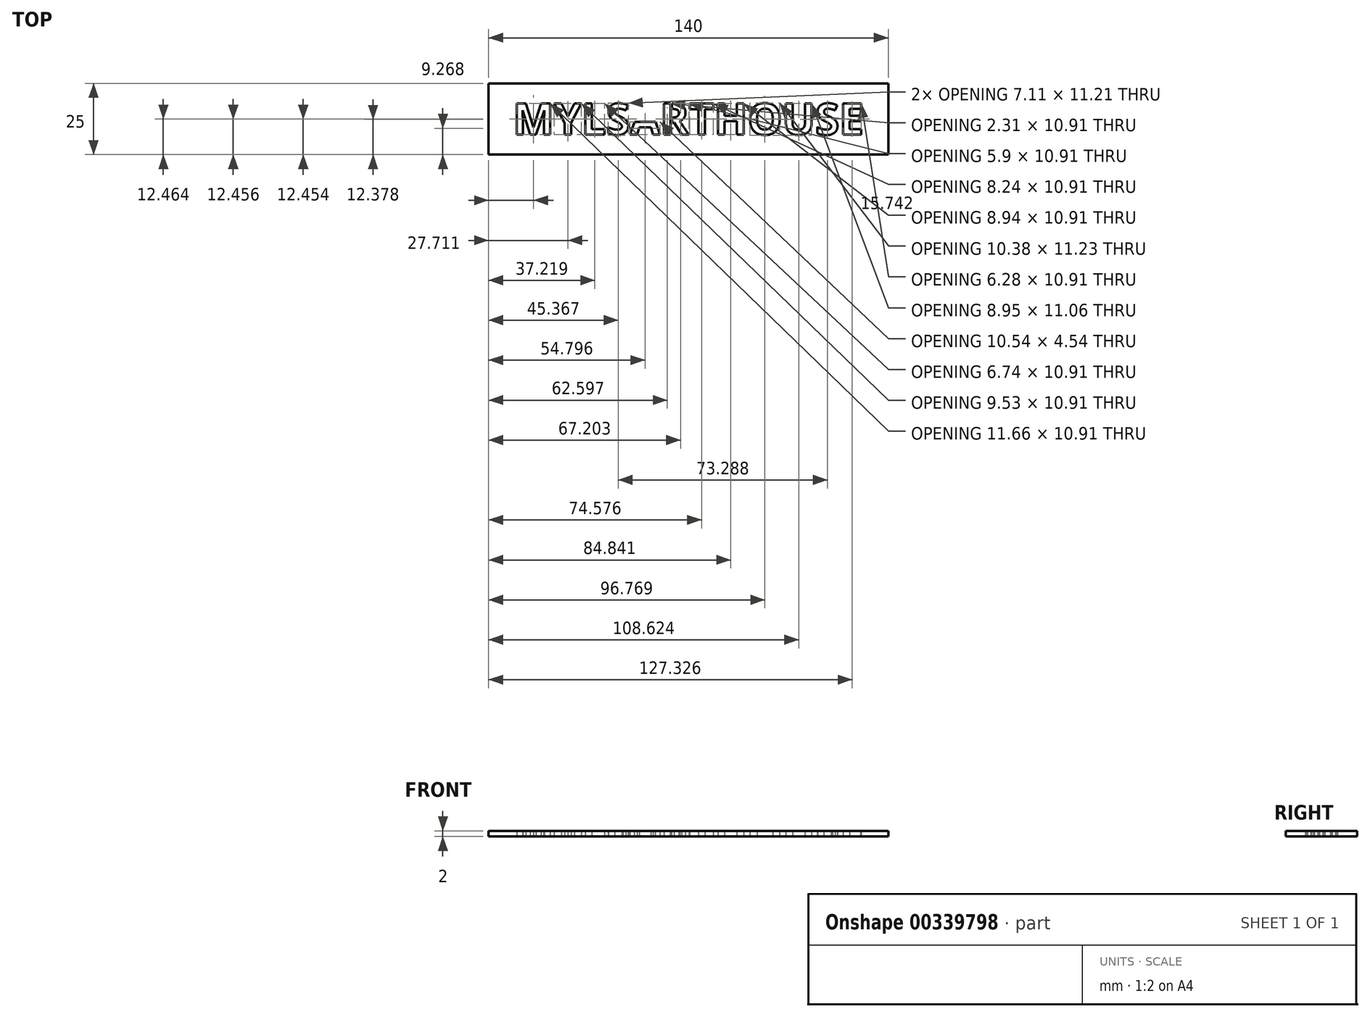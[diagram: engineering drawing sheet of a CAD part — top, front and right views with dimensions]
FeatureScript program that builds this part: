
annotation { "Feature Type Name" : "Feature", "Feature Type Description" : "" }
export const myFeature = defineFeature(function(context is Context, id is Id, definition is map)
    precondition{}
    {
        {
            var Q0;
            Q0=qCreatedBy(makeId("Top.planeOp"),FACE);
            var sketch = newSketch(context, id + "F0", { "sketchPlane" : qUnion([Q0])});
            skText(sketch, "E0", { "text": "MYLSARTHOUSE", "fontName": "OpenSans-Bold.ttf"});
            skLineSegment(sketch, "E1.bottom", {"start": v(70, -12.5) * mm, "end": v(-70, -12.5) * mm});
            skLineSegment(sketch, "E1.top", {"start": v(70, 12.5) * mm, "end": v(-70, 12.5) * mm});
            skLineSegment(sketch, "E1.left", {"start": v(70, -12.5) * mm, "end": v(70, 12.5) * mm});
            skLineSegment(sketch, "E1.right", {"start": v(-70, -12.5) * mm, "end": v(-70, 12.5) * mm});
            skPoint(sketch, "E1.middle", {"position": v(0, 0) * mm});
            const initialGuessF0  = {"E0": [-0.06146, -0.0055, 1, 0, 0.011]};
            skSetInitialGuess(sketch, initialGuessF0);
            skSolve(sketch);
        }
        {
            var Q0;
            Q0=makeQuery(id+"F0.imprint","IMPRINT",FACE,{"disambiguationData":[TD([[makeQuery(id+"F0.imprint","IMPRINT",EDGE,{"derivedFrom":sQuery(id+"F0.wireOp",EDGE,"E0.sketch_text.stroke-0")}),1.0]])]});
            var Q1;
            Q1=makeQuery(id+"F0.imprint","IMPRINT",FACE,{"disambiguationData":[TD([[makeQuery(id+"F0.imprint","IMPRINT",EDGE,{"derivedFrom":sQuery(id+"F0.wireOp",EDGE,"E0.sketch_text.stroke-74")}),1.0]])]});
            var Q2;
            Q2=makeQuery(id+"F0.imprint","IMPRINT",FACE,{"disambiguationData":[TD([[makeQuery(id+"F0.imprint","IMPRINT",EDGE,{"derivedFrom":sQuery(id+"F0.wireOp",EDGE,"E0.sketch_text.stroke-70")}),1.0]])]});
            var Q3;
            Q3 = qSketchRegion(id + "F0", true);
            var Q4;
            Q4=makeQuery(id+"F0.imprint","IMPRINT",FACE,{"disambiguationData":[TD([[makeQuery(id+"F0.imprint","IMPRINT",EDGE,{"derivedFrom":sQuery(id+"F0.wireOp",EDGE,"E0.sketch_text.stroke-121")}),1.0]])]});
            extrude(context, id + "F1", {"entities" : qUnion([Q0, Q1, Q2, Q3, Q4]), "depth" : 2 * mm});
        }
        {
            var Q0;
            Q0=makeQuery(id+"F1.opExtrude","CAP_FACE",FACE,{"disambiguationData":[OSD([sQuery(id+"F0.wireOp",EDGE,"E0.sketch_text.stroke-0"),sQuery(id+"F0.wireOp",EDGE,"E0.sketch_text.stroke-1"),sQuery(id+"F0.wireOp",EDGE,"E0.sketch_text.stroke-2"),sQuery(id+"F0.wireOp",EDGE,"E0.sketch_text.stroke-3"),sQuery(id+"F0.wireOp",EDGE,"E0.sketch_text.stroke-4"),sQuery(id+"F0.wireOp",EDGE,"E0.sketch_text.stroke-5"),sQuery(id+"F0.wireOp",EDGE,"E0.sketch_text.stroke-6"),sQuery(id+"F0.wireOp",EDGE,"E0.sketch_text.stroke-7"),sQuery(id+"F0.wireOp",EDGE,"E0.sketch_text.stroke-8"),sQuery(id+"F0.wireOp",EDGE,"E0.sketch_text.stroke-9"),sQuery(id+"F0.wireOp",EDGE,"E0.sketch_text.stroke-10"),sQuery(id+"F0.wireOp",EDGE,"E0.sketch_text.stroke-11"),sQuery(id+"F0.wireOp",EDGE,"E0.sketch_text.stroke-12"),sQuery(id+"F0.wireOp",EDGE,"E0.sketch_text.stroke-13"),sQuery(id+"F0.wireOp",EDGE,"E0.sketch_text.stroke-14"),sQuery(id+"F0.wireOp",EDGE,"E0.sketch_text.stroke-15"),sQuery(id+"F0.wireOp",EDGE,"E0.sketch_text.stroke-16"),sQuery(id+"F0.wireOp",EDGE,"E0.sketch_text.stroke-17"),sQuery(id+"F0.wireOp",EDGE,"E0.sketch_text.stroke-18"),sQuery(id+"F0.wireOp",EDGE,"E0.sketch_text.stroke-19"),sQuery(id+"F0.wireOp",EDGE,"E0.sketch_text.stroke-20"),sQuery(id+"F0.wireOp",EDGE,"E0.sketch_text.stroke-21"),sQuery(id+"F0.wireOp",EDGE,"E0.sketch_text.stroke-22"),sQuery(id+"F0.wireOp",EDGE,"E0.sketch_text.stroke-23"),sQuery(id+"F0.wireOp",EDGE,"E0.sketch_text.stroke-24"),sQuery(id+"F0.wireOp",EDGE,"E0.sketch_text.stroke-25"),sQuery(id+"F0.wireOp",EDGE,"E0.sketch_text.stroke-26"),sQuery(id+"F0.wireOp",EDGE,"E0.sketch_text.stroke-27"),sQuery(id+"F0.wireOp",EDGE,"E0.sketch_text.stroke-28"),sQuery(id+"F0.wireOp",EDGE,"E0.sketch_text.stroke-29"),sQuery(id+"F0.wireOp",EDGE,"E0.sketch_text.stroke-30"),sQuery(id+"F0.wireOp",EDGE,"E0.sketch_text.stroke-31"),sQuery(id+"F0.wireOp",EDGE,"E0.sketch_text.stroke-32"),sQuery(id+"F0.wireOp",EDGE,"E0.sketch_text.stroke-33"),sQuery(id+"F0.wireOp",EDGE,"E0.sketch_text.stroke-34"),sQuery(id+"F0.wireOp",EDGE,"E0.sketch_text.stroke-35"),sQuery(id+"F0.wireOp",EDGE,"E0.sketch_text.stroke-36"),sQuery(id+"F0.wireOp",EDGE,"E0.sketch_text.stroke-37"),sQuery(id+"F0.wireOp",EDGE,"E0.sketch_text.stroke-38"),sQuery(id+"F0.wireOp",EDGE,"E0.sketch_text.stroke-39"),sQuery(id+"F0.wireOp",EDGE,"E0.sketch_text.stroke-40"),sQuery(id+"F0.wireOp",EDGE,"E0.sketch_text.stroke-41"),sQuery(id+"F0.wireOp",EDGE,"E0.sketch_text.stroke-42"),sQuery(id+"F0.wireOp",EDGE,"E0.sketch_text.stroke-43"),sQuery(id+"F0.wireOp",EDGE,"E0.sketch_text.stroke-44"),sQuery(id+"F0.wireOp",EDGE,"E0.sketch_text.stroke-45"),sQuery(id+"F0.wireOp",EDGE,"E0.sketch_text.stroke-46"),sQuery(id+"F0.wireOp",EDGE,"E0.sketch_text.stroke-47"),sQuery(id+"F0.wireOp",EDGE,"E0.sketch_text.stroke-48"),sQuery(id+"F0.wireOp",EDGE,"E0.sketch_text.stroke-49"),sQuery(id+"F0.wireOp",EDGE,"E0.sketch_text.stroke-50"),sQuery(id+"F0.wireOp",EDGE,"E0.sketch_text.stroke-51"),sQuery(id+"F0.wireOp",EDGE,"E0.sketch_text.stroke-52"),sQuery(id+"F0.wireOp",EDGE,"E0.sketch_text.stroke-53"),sQuery(id+"F0.wireOp",EDGE,"E0.sketch_text.stroke-54"),sQuery(id+"F0.wireOp",EDGE,"E0.sketch_text.stroke-55"),sQuery(id+"F0.wireOp",EDGE,"E0.sketch_text.stroke-56"),sQuery(id+"F0.wireOp",EDGE,"E0.sketch_text.stroke-57"),sQuery(id+"F0.wireOp",EDGE,"E0.sketch_text.stroke-58"),sQuery(id+"F0.wireOp",EDGE,"E0.sketch_text.stroke-59"),sQuery(id+"F0.wireOp",EDGE,"E0.sketch_text.stroke-60"),sQuery(id+"F0.wireOp",EDGE,"E0.sketch_text.stroke-61"),sQuery(id+"F0.wireOp",EDGE,"E0.sketch_text.stroke-62"),sQuery(id+"F0.wireOp",EDGE,"E0.sketch_text.stroke-63"),sQuery(id+"F0.wireOp",EDGE,"E0.sketch_text.stroke-64"),sQuery(id+"F0.wireOp",EDGE,"E0.sketch_text.stroke-65"),sQuery(id+"F0.wireOp",EDGE,"E0.sketch_text.stroke-66"),sQuery(id+"F0.wireOp",EDGE,"E0.sketch_text.stroke-67"),sQuery(id+"F0.wireOp",EDGE,"E0.sketch_text.stroke-68"),sQuery(id+"F0.wireOp",EDGE,"E0.sketch_text.stroke-69"),sQuery(id+"F0.wireOp",EDGE,"E0.sketch_text.stroke-81"),sQuery(id+"F0.wireOp",EDGE,"E0.sketch_text.stroke-82"),sQuery(id+"F0.wireOp",EDGE,"E0.sketch_text.stroke-83"),sQuery(id+"F0.wireOp",EDGE,"E0.sketch_text.stroke-84"),sQuery(id+"F0.wireOp",EDGE,"E0.sketch_text.stroke-85"),sQuery(id+"F0.wireOp",EDGE,"E0.sketch_text.stroke-86"),sQuery(id+"F0.wireOp",EDGE,"E0.sketch_text.stroke-87"),sQuery(id+"F0.wireOp",EDGE,"E0.sketch_text.stroke-88"),sQuery(id+"F0.wireOp",EDGE,"E0.sketch_text.stroke-89"),sQuery(id+"F0.wireOp",EDGE,"E0.sketch_text.stroke-90"),sQuery(id+"F0.wireOp",EDGE,"E0.sketch_text.stroke-91"),sQuery(id+"F0.wireOp",EDGE,"E0.sketch_text.stroke-92"),sQuery(id+"F0.wireOp",EDGE,"E0.sketch_text.stroke-93"),sQuery(id+"F0.wireOp",EDGE,"E0.sketch_text.stroke-94"),sQuery(id+"F0.wireOp",EDGE,"E0.sketch_text.stroke-95"),sQuery(id+"F0.wireOp",EDGE,"E0.sketch_text.stroke-96"),sQuery(id+"F0.wireOp",EDGE,"E0.sketch_text.stroke-97"),sQuery(id+"F0.wireOp",EDGE,"E0.sketch_text.stroke-98"),sQuery(id+"F0.wireOp",EDGE,"E0.sketch_text.stroke-99"),sQuery(id+"F0.wireOp",EDGE,"E0.sketch_text.stroke-100"),sQuery(id+"F0.wireOp",EDGE,"E0.sketch_text.stroke-101"),sQuery(id+"F0.wireOp",EDGE,"E0.sketch_text.stroke-102"),sQuery(id+"F0.wireOp",EDGE,"E0.sketch_text.stroke-103"),sQuery(id+"F0.wireOp",EDGE,"E0.sketch_text.stroke-104"),sQuery(id+"F0.wireOp",EDGE,"E0.sketch_text.stroke-105"),sQuery(id+"F0.wireOp",EDGE,"E0.sketch_text.stroke-106"),sQuery(id+"F0.wireOp",EDGE,"E0.sketch_text.stroke-107"),sQuery(id+"F0.wireOp",EDGE,"E0.sketch_text.stroke-108"),sQuery(id+"F0.wireOp",EDGE,"E0.sketch_text.stroke-109"),sQuery(id+"F0.wireOp",EDGE,"E0.sketch_text.stroke-110"),sQuery(id+"F0.wireOp",EDGE,"E0.sketch_text.stroke-111"),sQuery(id+"F0.wireOp",EDGE,"E0.sketch_text.stroke-112"),sQuery(id+"F0.wireOp",EDGE,"E0.sketch_text.stroke-113"),sQuery(id+"F0.wireOp",EDGE,"E0.sketch_text.stroke-114"),sQuery(id+"F0.wireOp",EDGE,"E0.sketch_text.stroke-115"),sQuery(id+"F0.wireOp",EDGE,"E0.sketch_text.stroke-116"),sQuery(id+"F0.wireOp",EDGE,"E0.sketch_text.stroke-117"),sQuery(id+"F0.wireOp",EDGE,"E0.sketch_text.stroke-118"),sQuery(id+"F0.wireOp",EDGE,"E0.sketch_text.stroke-119"),sQuery(id+"F0.wireOp",EDGE,"E0.sketch_text.stroke-120"),sQuery(id+"F0.wireOp",EDGE,"E0.sketch_text.stroke-127"),sQuery(id+"F0.wireOp",EDGE,"E0.sketch_text.stroke-128"),sQuery(id+"F0.wireOp",EDGE,"E0.sketch_text.stroke-129"),sQuery(id+"F0.wireOp",EDGE,"E0.sketch_text.stroke-130"),sQuery(id+"F0.wireOp",EDGE,"E0.sketch_text.stroke-131"),sQuery(id+"F0.wireOp",EDGE,"E0.sketch_text.stroke-132"),sQuery(id+"F0.wireOp",EDGE,"E0.sketch_text.stroke-133"),sQuery(id+"F0.wireOp",EDGE,"E0.sketch_text.stroke-134"),sQuery(id+"F0.wireOp",EDGE,"E0.sketch_text.stroke-135"),sQuery(id+"F0.wireOp",EDGE,"E0.sketch_text.stroke-136"),sQuery(id+"F0.wireOp",EDGE,"E0.sketch_text.stroke-137"),sQuery(id+"F0.wireOp",EDGE,"E0.sketch_text.stroke-138"),sQuery(id+"F0.wireOp",EDGE,"E0.sketch_text.stroke-139"),sQuery(id+"F0.wireOp",EDGE,"E0.sketch_text.stroke-140"),sQuery(id+"F0.wireOp",EDGE,"E0.sketch_text.stroke-141"),sQuery(id+"F0.wireOp",EDGE,"E0.sketch_text.stroke-142"),sQuery(id+"F0.wireOp",EDGE,"E0.sketch_text.stroke-143"),sQuery(id+"F0.wireOp",EDGE,"E0.sketch_text.stroke-144"),sQuery(id+"F0.wireOp",EDGE,"E0.sketch_text.stroke-145"),sQuery(id+"F0.wireOp",EDGE,"E0.sketch_text.stroke-146"),sQuery(id+"F0.wireOp",EDGE,"E0.sketch_text.stroke-147"),sQuery(id+"F0.wireOp",EDGE,"E0.sketch_text.stroke-148"),sQuery(id+"F0.wireOp",EDGE,"E0.sketch_text.stroke-149"),sQuery(id+"F0.wireOp",EDGE,"E0.sketch_text.stroke-150"),sQuery(id+"F0.wireOp",EDGE,"E0.sketch_text.stroke-151"),sQuery(id+"F0.wireOp",EDGE,"E0.sketch_text.stroke-152"),sQuery(id+"F0.wireOp",EDGE,"E0.sketch_text.stroke-153"),sQuery(id+"F0.wireOp",EDGE,"E0.sketch_text.stroke-154"),sQuery(id+"F0.wireOp",EDGE,"E0.sketch_text.stroke-155"),sQuery(id+"F0.wireOp",EDGE,"E0.sketch_text.stroke-156"),sQuery(id+"F0.wireOp",EDGE,"E0.sketch_text.stroke-157"),sQuery(id+"F0.wireOp",EDGE,"E0.sketch_text.stroke-158"),sQuery(id+"F0.wireOp",EDGE,"E0.sketch_text.stroke-159"),sQuery(id+"F0.wireOp",EDGE,"E0.sketch_text.stroke-160"),sQuery(id+"F0.wireOp",EDGE,"E0.sketch_text.stroke-161"),sQuery(id+"F0.wireOp",EDGE,"E0.sketch_text.stroke-162"),sQuery(id+"F0.wireOp",EDGE,"E0.sketch_text.stroke-163"),sQuery(id+"F0.wireOp",EDGE,"E0.sketch_text.stroke-164"),sQuery(id+"F0.wireOp",EDGE,"E0.sketch_text.stroke-165"),sQuery(id+"F0.wireOp",EDGE,"E0.sketch_text.stroke-166"),sQuery(id+"F0.wireOp",EDGE,"E0.sketch_text.stroke-167"),sQuery(id+"F0.wireOp",EDGE,"E0.sketch_text.stroke-168"),sQuery(id+"F0.wireOp",EDGE,"E0.sketch_text.stroke-169"),sQuery(id+"F0.wireOp",EDGE,"E0.sketch_text.stroke-170"),sQuery(id+"F0.wireOp",EDGE,"E0.sketch_text.stroke-171"),sQuery(id+"F0.wireOp",EDGE,"E0.sketch_text.stroke-172"),sQuery(id+"F0.wireOp",EDGE,"E0.sketch_text.stroke-173"),sQuery(id+"F0.wireOp",EDGE,"E0.sketch_text.stroke-174"),sQuery(id+"F0.wireOp",EDGE,"E0.sketch_text.stroke-175"),sQuery(id+"F0.wireOp",EDGE,"E0.sketch_text.stroke-176"),sQuery(id+"F0.wireOp",EDGE,"E0.sketch_text.stroke-177"),sQuery(id+"F0.wireOp",EDGE,"E0.sketch_text.stroke-178"),sQuery(id+"F0.wireOp",EDGE,"E0.sketch_text.stroke-179"),sQuery(id+"F0.wireOp",EDGE,"E0.sketch_text.stroke-180"),sQuery(id+"F0.wireOp",EDGE,"E0.sketch_text.stroke-181"),sQuery(id+"F0.wireOp",EDGE,"E1.bottom"),sQuery(id+"F0.wireOp",EDGE,"E1.top"),sQuery(id+"F0.wireOp",EDGE,"E1.left"),sQuery(id+"F0.wireOp",EDGE,"E1.right")])],"isStart":false});
            var sketch = newSketch(context, id + "F2", { "sketchPlane" : qUnion([Q0])});
            skLineSegment(sketch, "E2.0", {"start": v(-16.6, -0.96) * mm, "end": v(-13.77, -0.96) * mm});
            skLineSegment(sketch, "E3.0", {"start": v(-13.8, 5.45) * mm, "end": v(-9.93, -5.5) * mm});
            skLineSegment(sketch, "E4.0", {"start": v(-20.47, -5.5) * mm, "end": v(-16.62, 5.45) * mm});
            skLineSegment(sketch, "E5.0", {"start": v(-16.62, 5.45) * mm, "end": v(-13.8, 5.45) * mm});
            skLineSegment(sketch, "E6.0.0", {"start": v(-5.54, 3.51) * mm, "end": v(-6.25, 3.51) * mm});
            skLineSegment(sketch, "E6.0.1", {"start": v(-6.25, 3.51) * mm, "end": v(-6.25, 0.57) * mm});
            skLineSegment(sketch, "E6.0.2", {"start": v(-6.25, 0.57) * mm, "end": v(-5.5, 0.57) * mm});
            skFitSpline(sketch, "E6.0.3", {"points": [v(-5.5, 0.57) * mm, v(-4.4, 0.57) * mm, v(-3.88, 0.93) * mm]});
            skFitSpline(sketch, "E6.0.4", {"points": [v(-3.88, 0.93) * mm, v(-3.36, 1.3) * mm, v(-3.36, 2.08) * mm]});
            skFitSpline(sketch, "E6.0.5", {"points": [v(-3.36, 2.08) * mm, v(-3.36, 2.86) * mm, v(-3.9, 3.18) * mm]});
            skFitSpline(sketch, "E6.0.6", {"points": [v(-3.9, 3.18) * mm, v(-4.43, 3.51) * mm, v(-5.54, 3.51) * mm]});
            skFitSpline(sketch, "E7.0.0", {"points": [v(-15.2, 3.76) * mm, v(-15.45, 2.8) * mm, v(-16.6, -0.96) * mm]});
            skFitSpline(sketch, "E7.0.2", {"points": [v(-13.77, -0.96) * mm, v(-14.86, 2.56) * mm, v(-15, 3.03) * mm]});
            skFitSpline(sketch, "E7.0.3", {"points": [v(-15, 3.03) * mm, v(-15.14, 3.5) * mm, v(-15.2, 3.76) * mm]});
            skLineSegment(sketch, "E8.0", {"start": v(-5.02, -1.32) * mm, "end": v(-6.25, -1.32) * mm});
            skFitSpline(sketch, "E9.0", {"points": [v(-2.1, 4.6) * mm, v(-1.03, 3.79) * mm, v(-1.03, 2.14) * mm]});
            skFitSpline(sketch, "E10.0", {"points": [v(-1.03, 2.14) * mm, v(-1.03, 1.18) * mm, v(-1.55, 0.43) * mm]});
            skLineSegment(sketch, "E11.0", {"start": v(-8.56, 5.4) * mm, "end": v(-5.38, 5.4) * mm});
            skFitSpline(sketch, "E12.0.0", {"points": [v(26.79, 3.65) * mm, v(25.4, 3.65) * mm, v(24.7, 2.72) * mm]});
            skFitSpline(sketch, "E12.0.1", {"points": [v(24.7, 2.72) * mm, v(24, 1.8) * mm, v(24, -0.03) * mm]});
            skFitSpline(sketch, "E12.0.2", {"points": [v(24, -0.03) * mm, v(24, -1.86) * mm, v(24.7, -2.78) * mm]});
            skFitSpline(sketch, "E12.0.3", {"points": [v(24.7, -2.78) * mm, v(25.4, -3.7) * mm, v(26.77, -3.7) * mm]});
            skFitSpline(sketch, "E12.0.4", {"points": [v(26.77, -3.7) * mm, v(29.54, -3.7) * mm, v(29.54, -0.03) * mm]});
            skFitSpline(sketch, "E12.0.5", {"points": [v(29.54, -0.03) * mm, v(29.54, 3.65) * mm, v(26.79, 3.65) * mm]});
            skFitSpline(sketch, "E13.0", {"points": [v(31.96, -0.03) * mm, v(31.96, -2.74) * mm, v(30.62, -4.2) * mm]});
            skFitSpline(sketch, "E14.0", {"points": [v(30.63, 4.13) * mm, v(31.96, 2.68) * mm, v(31.96, -0.03) * mm]});
            skFitSpline(sketch, "E15.0", {"points": [v(26.79, 5.58) * mm, v(29.3, 5.58) * mm, v(30.63, 4.13) * mm]});
            skFitSpline(sketch, "E16.0", {"points": [v(22.93, 4.14) * mm, v(24.27, 5.58) * mm, v(26.79, 5.58) * mm]});
            skFitSpline(sketch, "E17.0", {"points": [v(21.58, -0.02) * mm, v(21.58, 2.7) * mm, v(22.93, 4.14) * mm]});
            skFitSpline(sketch, "E18.0", {"points": [v(22.92, -4.2) * mm, v(21.58, -2.74) * mm, v(21.58, -0.02) * mm]});
            skFitSpline(sketch, "E19.0", {"points": [v(26.77, -5.65) * mm, v(24.26, -5.65) * mm, v(22.92, -4.2) * mm]});
            skFitSpline(sketch, "E20.0", {"points": [v(30.62, -4.2) * mm, v(29.28, -5.65) * mm, v(26.77, -5.65) * mm]});
            skArc(sketch, "E21.0.startCap", {"start": v(27.04, 3.65) * mm, "mid": v(27.04, 3.65) * mm, "end": v(27.03, 3.64) * mm});
            skLineSegment(sketch, "E21.0.left", {"start": v(26.54, 3.65) * mm, "end": v(26.54, 5.58) * mm});
            skLineSegment(sketch, "E21.0.right", {"start": v(27.04, 3.65) * mm, "end": v(27.04, 5.58) * mm});
            skArc(sketch, "E22.0.endCap", {"start": v(24, 0.22) * mm, "mid": v(24, 0.22) * mm, "end": v(24, 0.22) * mm});
            skLineSegment(sketch, "E22.0.left", {"start": v(21.58, 0.23) * mm, "end": v(24, 0.22) * mm});
            skLineSegment(sketch, "E22.0.right", {"start": v(21.58, -0.27) * mm, "end": v(24, -0.28) * mm});
            skArc(sketch, "E22.1.startCap", {"start": v(26.52, -3.7) * mm, "mid": v(26.52, -3.7) * mm, "end": v(26.52, -3.7) * mm});
            skLineSegment(sketch, "E22.1.left", {"start": v(27.02, -3.7) * mm, "end": v(27.02, -5.65) * mm});
            skLineSegment(sketch, "E22.1.right", {"start": v(26.52, -3.7) * mm, "end": v(26.52, -5.65) * mm});
            skArc(sketch, "E22.2.startCap", {"start": v(29.54, -0.28) * mm, "mid": v(29.54, -0.28) * mm, "end": v(29.53, -0.28) * mm});
            skLineSegment(sketch, "E22.2.left", {"start": v(29.54, 0.22) * mm, "end": v(31.96, 0.22) * mm});
            skLineSegment(sketch, "E22.2.right", {"start": v(29.54, -0.28) * mm, "end": v(31.96, -0.28) * mm});
            skArc(sketch, "E23.trimOffspring", {"start": v(24, -0.28) * mm, "mid": v(24, -0.28) * mm, "end": v(24, -0.28) * mm});
            skArc(sketch, "E24.trimOffspring", {"start": v(29.53, 0.22) * mm, "mid": v(29.54, 0.22) * mm, "end": v(29.54, 0.22) * mm});
            skArc(sketch, "E25.trimOffspring", {"start": v(27.02, -3.7) * mm, "mid": v(27.02, -3.7) * mm, "end": v(27.02, -3.7) * mm});
            skArc(sketch, "E26.trimOffspring", {"start": v(26.54, 3.64) * mm, "mid": v(26.54, 3.65) * mm, "end": v(26.54, 3.65) * mm});
            skLineSegment(sketch, "E27", {"start": v(-6.25, 3.51) * mm, "end": v(-6.25, 5.4) * mm});
            skLineSegment(sketch, "E28", {"start": v(-6.25, 5.4) * mm, "end": v(-5.75, 5.4) * mm});
            skLineSegment(sketch, "E29", {"start": v(-5.75, 5.4) * mm, "end": v(-5.75, 3.51) * mm});
            skLineSegment(sketch, "E30", {"start": v(-6.25, 0.57) * mm, "end": v(-6.25, -1.32) * mm});
            skLineSegment(sketch, "E31", {"start": v(-5.75, 0.57) * mm, "end": v(-5.75, -1.32) * mm});
            skArc(sketch, "E32.0.startCap", {"start": v(-3.36, 1.83) * mm, "mid": v(-3.37, 1.83) * mm, "end": v(-3.37, 1.83) * mm});
            skLineSegment(sketch, "E32.0.left", {"start": v(-3.36, 2.33) * mm, "end": v(-1.03, 2.33) * mm});
            skLineSegment(sketch, "E32.0.right", {"start": v(-3.36, 1.83) * mm, "end": v(-1.03, 1.83) * mm});
            skArc(sketch, "E33.trimOffspring", {"start": v(-3.38, 2.33) * mm, "mid": v(-3.37, 2.33) * mm, "end": v(-3.36, 2.33) * mm});
            skPoint(sketch, "E34.end.orphan", {"position": v(-1.03, 2.08) * mm});
            skLineSegment(sketch, "E35", {"start": v(-13.77, -0.96) * mm, "end": v(-11.53, -0.96) * mm});
            skLineSegment(sketch, "E36", {"start": v(-16.6, -0.96) * mm, "end": v(-18.88, -0.96) * mm});
            skLineSegment(sketch, "E37", {"start": v(-16.45, -0.46) * mm, "end": v(-18.7, -0.46) * mm});
            skLineSegment(sketch, "E38", {"start": v(-13.92, -0.46) * mm, "end": v(-11.7, -0.46) * mm});
            skLineSegment(sketch, "E39", {"start": v(-15.2, 5.45) * mm, "end": v(-14.95, 5.45) * mm});
            skLineSegment(sketch, "E40", {"start": v(-14.95, 5.45) * mm, "end": v(-14.95, 2.86) * mm});
            skLineSegment(sketch, "E41", {"start": v(-15.45, 5.45) * mm, "end": v(-15.45, 2.86) * mm});
            skSolve(sketch);
        }
        {
            var Q0;
            {var subQ0=sQuery(id+"F2.wireOp",EDGE,"E7.0.3");Q0=makeQuery(id+"F2.imprint","IMPRINT",FACE,{"disambiguationData":[TD([[makeQuery(id+"F2.imprint","IMPRINT",EDGE,{"derivedFrom":subQ0}),-1.0]])]});}
            var Q1;
            {var subQ0=sQuery(id+"F2.wireOp",EDGE,"E36");Q1=makeQuery(id+"F2.imprint","IMPRINT",FACE,{"disambiguationData":[TD([[makeQuery(id+"F2.imprint","IMPRINT",EDGE,{"derivedFrom":subQ0}),-1.0]])]});}
            var Q2;
            {var subQ0=sQuery(id+"F2.wireOp",EDGE,"E35");Q2=makeQuery(id+"F2.imprint","IMPRINT",FACE,{"disambiguationData":[TD([[makeQuery(id+"F2.imprint","IMPRINT",EDGE,{"derivedFrom":subQ0}),1.0]])]});}
            var Q3;
            {var subQ0=sQuery(id+"F2.wireOp",EDGE,"E27");Q3=makeQuery(id+"F2.imprint","IMPRINT",FACE,{"disambiguationData":[TD([[makeQuery(id+"F2.imprint","IMPRINT",EDGE,{"derivedFrom":subQ0}),-1.0]])]});}
            var Q4;
            {var subQ5=sQuery(id+"F2.wireOp",EDGE,"E32.0.startCap");Q4=makeQuery(id+"F2.imprint","IMPRINT",FACE,{"disambiguationData":[TD([[makeQuery(id+"F2.imprint","IMPRINT",EDGE,{"derivedFrom":subQ5}),-1.0]])]});}
            var Q5;
            {var subQ0=sQuery(id+"F2.wireOp",EDGE,"E30");Q5=makeQuery(id+"F2.imprint","IMPRINT",FACE,{"disambiguationData":[TD([[makeQuery(id+"F2.imprint","IMPRINT",EDGE,{"derivedFrom":subQ0}),1.0]])]});}
            var Q6;
            {var subQ5=sQuery(id+"F2.wireOp",EDGE,"E22.2.startCap");Q6=makeQuery(id+"F2.imprint","IMPRINT",FACE,{"disambiguationData":[TD([[makeQuery(id+"F2.imprint","IMPRINT",EDGE,{"derivedFrom":subQ5}),-1.0]])]});}
            var Q7;
            {var subQ6=sQuery(id+"F2.wireOp",EDGE,"E21.0.startCap");Q7=makeQuery(id+"F2.imprint","IMPRINT",FACE,{"disambiguationData":[TD([[makeQuery(id+"F2.imprint","IMPRINT",EDGE,{"derivedFrom":subQ6}),-1.0]])]});}
            var Q8;
            {var subQ8=sQuery(id+"F2.wireOp",EDGE,"E22.0.endCap");Q8=makeQuery(id+"F2.imprint","IMPRINT",FACE,{"disambiguationData":[TD([[makeQuery(id+"F2.imprint","IMPRINT",EDGE,{"derivedFrom":subQ8}),-1.0]])]});}
            var Q9;
            {var subQ8=sQuery(id+"F2.wireOp",EDGE,"E22.1.startCap");Q9=makeQuery(id+"F2.imprint","IMPRINT",FACE,{"disambiguationData":[TD([[makeQuery(id+"F2.imprint","IMPRINT",EDGE,{"derivedFrom":subQ8}),-1.0]])]});}
            extrude(context, id + "F3", {"entities" : qUnion([Q0, Q1, Q2, Q3, Q4, Q5, Q6, Q7, Q8, Q9]), "operationType" : NewBodyOperationType.ADD, "oppositeDirection" : true, "depth" : 2 * mm});
        }
    });
